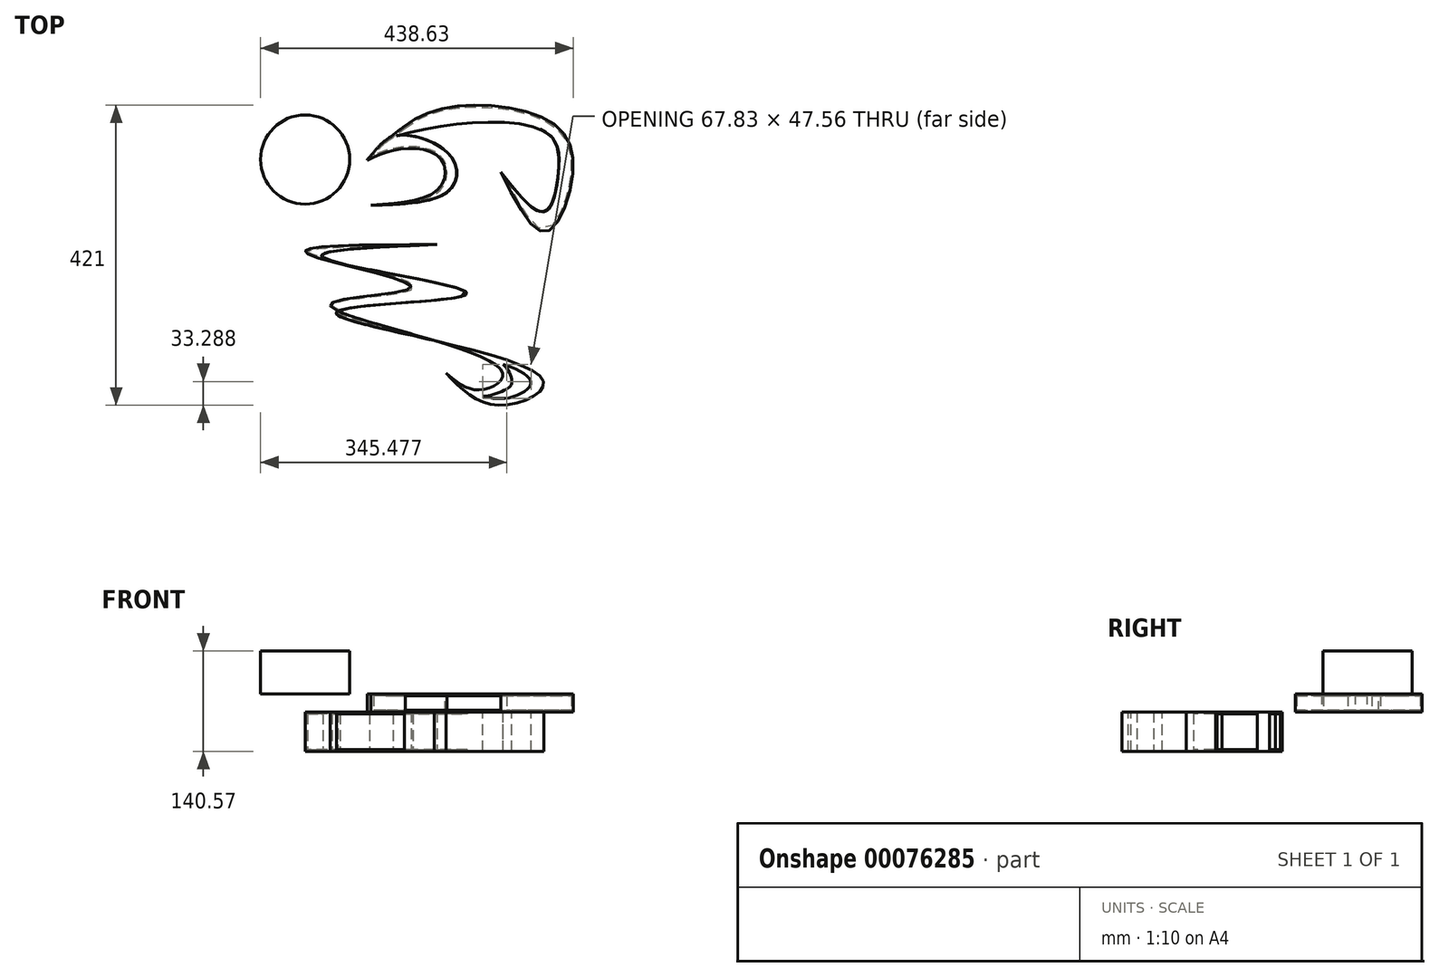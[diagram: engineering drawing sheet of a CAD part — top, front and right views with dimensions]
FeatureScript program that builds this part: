
annotation { "Feature Type Name" : "Feature", "Feature Type Description" : "" }
export const myFeature = defineFeature(function(context is Context, id is Id, definition is map)
    precondition{}
    {
        {
            var Q0;
            Q0=qCreatedBy(makeId("Top.planeOp"),FACE);
            var sketch = newSketch(context, id + "F0", { "sketchPlane" : qUnion([Q0])});
            skFitSpline(sketch, "E0", {"points": [v(26.78, 43.6) * mm, v(-131.32, 24.2) * mm, v(68.9, -25.6) * mm, v(-114.66, -51.9) * mm, v(173.44, -143.65) * mm, v(117.93, -181.76) * mm, v(39.3, -136.8) * mm], "startDerivative": vector(-1645.07, -67.99) * mm, "endDerivative": vector(-525.07, 549.7) * mm});
            skFitSpline(sketch, "E1", {"points": [v(26.78, 43.6) * mm, v(-154.55, 30.31) * mm, v(-9.93, -16.29) * mm, v(-123.3, -40.59) * mm, v(116.53, -132.19) * mm, v(89.53, -160.01) * mm, v(39.3, -136.8) * mm], "startDerivative": vector(-1513.22, -1.63) * mm, "endDerivative": vector(-405.32, 341.5) * mm});
            skSolve(sketch);
        }
        {
            var Q0;
            {var subQ0=sQuery(id+"F0.wireOp",EDGE,"E1");var subQ1=sQuery(id+"F0.wireOp",EDGE,"E0");var subQ2=makeQuery(id+"F0.imprint","INTERSECT",VERTEX,{"disambiguationData":[OD(0.0)],"derivedFrom":[subQ1,subQ0]});Q0=makeQuery(id+"F0.imprint","IMPRINT",FACE,{"disambiguationData":[TD([[makeQuery(id+"F0.imprint","IMPRINT",EDGE,{"disambiguationData":[TD([[subQ2,-1.0]])],"derivedFrom":subQ1}),-1.0]])]});}
            var Q1;
            {var subQ0=sQuery(id+"F0.wireOp",EDGE,"E1");var subQ1=sQuery(id+"F0.wireOp",EDGE,"E0");var subQ2=makeQuery(id+"F0.imprint","INTERSECT",VERTEX,{"disambiguationData":[OD(1.0)],"derivedFrom":[subQ1,subQ0]});Q1=makeQuery(id+"F0.imprint","IMPRINT",FACE,{"disambiguationData":[TD([[makeQuery(id+"F0.imprint","IMPRINT",EDGE,{"disambiguationData":[TD([[subQ2,1.0]])],"derivedFrom":subQ1}),-1.0]])]});}
            var Q2;
            {var subQ0=sQuery(id+"F0.wireOp",EDGE,"E1");var subQ1=sQuery(id+"F0.wireOp",EDGE,"E0");var subQ2=makeQuery(id+"F0.imprint","INTERSECT",VERTEX,{"disambiguationData":[OD(2.0)],"derivedFrom":[subQ1,subQ0]});Q2=makeQuery(id+"F0.imprint","IMPRINT",FACE,{"disambiguationData":[TD([[makeQuery(id+"F0.imprint","IMPRINT",EDGE,{"disambiguationData":[TD([[subQ2,-1.0]])],"derivedFrom":subQ1}),1.0]])]});}
            extrude(context, id + "F1", {"entities" : qUnion([Q0, Q1, Q2]), "depth" : 55.24 * mm});
        }
        {
            var Q0;
            {var subQ0=sQuery(id+"F0.wireOp",EDGE,"E1");var subQ1=sQuery(id+"F0.wireOp",EDGE,"E0");var subQ2=makeQuery(id+"F0.imprint","INTERSECT",VERTEX,{"disambiguationData":[OD(1.0)],"derivedFrom":[subQ1,subQ0]});Q0=makeQuery(id+"F1.opExtrude","CAP_FACE",FACE,{"disambiguationData":[OSD([subQ1,subQ0]),TDD([makeQuery(id+"F0.imprint","IMPRINT",EDGE,{"disambiguationData":[TD([[subQ2,1.0]])],"derivedFrom":subQ1}),makeQuery(id+"F0.imprint","IMPRINT",EDGE,{"disambiguationData":[TD([[subQ2,1.0]])],"derivedFrom":subQ0})])],"isStart":false});}
            var sketch = newSketch(context, id + "F2", { "sketchPlane" : qUnion([Q0])});
            skFitSpline(sketch, "E2", {"points": [v(90.62, -169.13) * mm, v(124.26, -159.04) * mm, v(131.66, -148.95) * mm, v(119.55, -124.73) * mm], "startDerivative": vector(85.12, -0.81) * mm, "endDerivative": vector(-57.45, 42.52) * mm});
            skFitSpline(sketch, "E3", {"points": [v(119.55, -124.73) * mm, v(158.36, -148.95) * mm, v(131.66, -170.32) * mm, v(90.62, -169.13) * mm], "startDerivative": vector(118.96, -31.16) * mm, "endDerivative": vector(-109.21, 27.14) * mm});
            skSolve(sketch);
        }
        {
            var Q0;
            Q0=makeQuery(id+"F2.imprint","IMPRINT",FACE,{"disambiguationData":[TD([[makeQuery(id+"F2.imprint","IMPRINT",EDGE,{"derivedFrom":sQuery(id+"F2.wireOp",EDGE,"E2")}),-1.0]])]});
            extrude(context, id + "F3", {"entities" : qUnion([Q0]), "operationType" : NewBodyOperationType.REMOVE, "oppositeDirection" : true, "depth" : 90.38 * mm});
        }
        {
            var Q0;
            {var subQ0=sQuery(id+"F0.wireOp",EDGE,"E1");var subQ1=sQuery(id+"F0.wireOp",EDGE,"E0");Q0=makeQuery(id+"F1.opExtrude","SWEPT_FACE",FACE,{"disambiguationData":[OSD([subQ1]),TDD([makeQuery(id+"F0.imprint","IMPRINT",EDGE,{"disambiguationData":[TD([[makeQuery(id+"F0.imprint","INTERSECT",VERTEX,{"disambiguationData":[OD(0.0)],"derivedFrom":[subQ1,subQ0]}),-1.0]])],"derivedFrom":subQ1})])]});}
            shell(context, id + "F4", {"entities" : qUnion([Q0]), "thickness" : 2.54 * mm});
        }
        {
            var Q0;
            {var subQ0=sQuery(id+"F0.wireOp",EDGE,"E1");var subQ1=sQuery(id+"F0.wireOp",EDGE,"E0");Q0=makeQuery(id+"F1.opExtrude","SWEPT_FACE",FACE,{"disambiguationData":[OSD([subQ1]),TDD([makeQuery(id+"F0.imprint","IMPRINT",EDGE,{"disambiguationData":[TD([[makeQuery(id+"F0.imprint","INTERSECT",VERTEX,{"disambiguationData":[OD(2.0)],"derivedFrom":[subQ1,subQ0]}),-1.0]])],"derivedFrom":subQ1})])]});}
            shell(context, id + "F5", {"entities" : qUnion([Q0]), "thickness" : 2.54 * mm});
        }
        {
            var Q0;
            {var subQ0=sQuery(id+"F0.wireOp",EDGE,"E1");var subQ1=sQuery(id+"F0.wireOp",EDGE,"E0");var subQ2=makeQuery(id+"F0.imprint","INTERSECT",VERTEX,{"disambiguationData":[OD(0.0)],"derivedFrom":[subQ1,subQ0]});Q0=makeQuery(id+"F1.opExtrude","CAP_FACE",FACE,{"disambiguationData":[OSD([subQ1,subQ0]),TDD([makeQuery(id+"F0.imprint","IMPRINT",EDGE,{"disambiguationData":[TD([[subQ2,-1.0]])],"derivedFrom":subQ1}),makeQuery(id+"F0.imprint","IMPRINT",EDGE,{"disambiguationData":[TD([[subQ2,-1.0]])],"derivedFrom":subQ0})])],"isStart":false});}
            var sketch = newSketch(context, id + "F6", { "sketchPlane" : qUnion([Q0])});
            skFitSpline(sketch, "E4", {"points": [v(-65.96, 98.8) * mm, v(30.1, 123.03) * mm, v(31.75, 163.97) * mm, v(-20.17, 178.17) * mm, v(-71.4, 162.04) * mm], "startDerivative": vector(377.45, 28.05) * mm, "endDerivative": vector(-210.04, -102.41) * mm});
            skFitSpline(sketch, "E5", {"points": [v(-65.96, 98.8) * mm, v(44.2, 120.06) * mm, v(46.7, 166.54) * mm, v(-30.16, 196.33) * mm, v(-71.4, 162.04) * mm], "startDerivative": vector(440.55, 11.6) * mm, "endDerivative": vector(-187.8, -214.05) * mm});
            skFitSpline(sketch, "E6", {"points": [v(-30.16, 196.33) * mm, v(90.76, 215.22) * mm, v(185.83, 196.33) * mm, v(196.72, 141.73) * mm, v(177.16, 89.5) * mm, v(116.18, 145.35) * mm], "startDerivative": vector(456.71, 111.86) * mm, "endDerivative": vector(-344.36, 440.43) * mm});
            skFitSpline(sketch, "E7", {"points": [v(-57.84, 177.5) * mm, v(7.33, 225.42) * mm, v(105.9, 238.07) * mm, v(199.17, 205.5) * mm, v(215.93, 134.41) * mm, v(179.04, 61.5) * mm, v(116.18, 145.35) * mm], "startDerivative": vector(419.9, 344.3) * mm, "endDerivative": vector(-362.94, 721.68) * mm});
            skLineSegment(sketch, "E8", {"start": v(-30.16, 196.33) * mm, "end": v(-57.84, 177.5) * mm});
            skSolve(sketch);
        }
        {
            var Q0;
            {var subQ4=sQuery(id+"F6.wireOp",EDGE,"E4");Q0=makeQuery(id+"F6.imprint","IMPRINT",FACE,{"disambiguationData":[TD([[makeQuery(id+"F6.imprint","IMPRINT",EDGE,{"derivedFrom":subQ4}),-1.0]])]});}
            var Q1;
            {var subQ0=sQuery(id+"F6.wireOp",EDGE,"E8");Q1=makeQuery(id+"F6.imprint","IMPRINT",FACE,{"disambiguationData":[TD([[makeQuery(id+"F6.imprint","IMPRINT",EDGE,{"derivedFrom":subQ0}),-1.0]])]});}
            var Q2;
            {var subQ0=sQuery(id+"F6.wireOp",EDGE,"E6");Q2=makeQuery(id+"F6.imprint","IMPRINT",FACE,{"disambiguationData":[TD([[makeQuery(id+"F6.imprint","IMPRINT",EDGE,{"derivedFrom":subQ0}),1.0]])]});}
            extrude(context, id + "F7", {"entities" : qUnion([Q0, Q1, Q2]), "depth" : 25.4 * mm});
        }
        {
            var Q0;
            Q0=makeQuery(id+"F7.opExtrude","SWEPT_EDGE",EDGE,{"disambiguationData":[OSD([sQuery(id+"F6.wireOp",EDGE,"E5"),sQuery(id+"F6.wireOp",EDGE,"E7")])]});
            fillet(context, id + "F8", {"entities" : qUnion([Q0]), "radius" : 3168.65 * mm, "tangentPropagation" : true, "allowEdgeOverflow" : false});
        }
        {
            var Q0;
            Q0=makeQuery(id+"F7.opExtrude","SWEPT_FACE",FACE,{"disambiguationData":[OSD([sQuery(id+"F6.wireOp",EDGE,"E6")])]});
            var Q1;
            {var subQ0=sQuery(id+"F6.wireOp",EDGE,"E5");Q1=makeQuery(id+"F7.opExtrude","SWEPT_FACE",FACE,{"disambiguationData":[OSD([subQ0]),TDD([makeQuery(id+"F6.imprint","IMPRINT",EDGE,{"disambiguationData":[TD([[makeQuery(id+"F6.imprint","INTERSECT",VERTEX,{"disambiguationData":[OD(0.0)],"derivedFrom":[sQuery(id+"F6.wireOp",EDGE,"E4"),subQ0]}),-1.0]])],"derivedFrom":subQ0})])]});}
            shell(context, id + "F9", {"entities" : qUnion([Q0, Q1]), "thickness" : 2.54 * mm});
        }
        {
            var Q0;
            Q0=makeQuery(id+"F7.opExtrude","CAP_FACE",FACE,{"disambiguationData":[OSD([sQuery(id+"F6.wireOp",EDGE,"E4"),sQuery(id+"F6.wireOp",EDGE,"E5"),sQuery(id+"F6.wireOp",EDGE,"E6"),sQuery(id+"F6.wireOp",EDGE,"E7")])],"isStart":false});
            var sketch = newSketch(context, id + "F10", { "sketchPlane" : qUnion([Q0])});
            skCircle(sketch, "E9", {"center": v(-158.4, 162.9) * mm, "radius": 62.53 * mm});
            skSolve(sketch);
        }
        {
            var Q0;
            Q0=makeQuery(id+"F10.imprint","IMPRINT",FACE,{"disambiguationData":[TD([[makeQuery(id+"F10.imprint","IMPRINT",EDGE,{"derivedFrom":sQuery(id+"F10.wireOp",EDGE,"E9")}),1.0]])]});
            extrude(context, id + "F11", {"entities" : qUnion([Q0]), "depth" : 59.93 * mm});
        }
    });
